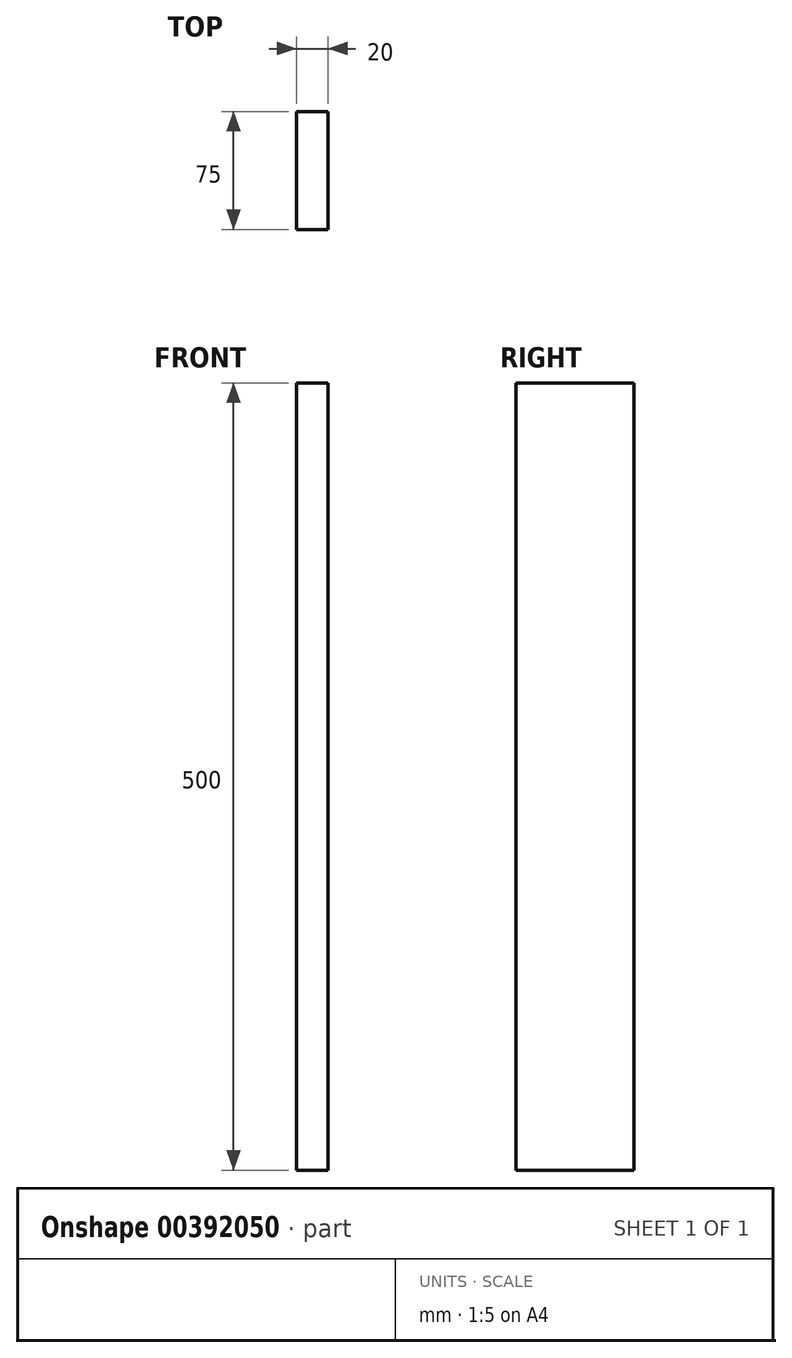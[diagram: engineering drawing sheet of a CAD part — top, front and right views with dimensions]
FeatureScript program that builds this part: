
annotation { "Feature Type Name" : "Feature", "Feature Type Description" : "" }
export const myFeature = defineFeature(function(context is Context, id is Id, definition is map)
    precondition{}
    {
        {
            var Q0;
            Q0=qCreatedBy(makeId("Top.planeOp"),FACE);
            var sketch = newSketch(context, id + "F0", { "sketchPlane" : qUnion([Q0])});
            skLineSegment(sketch, "E0.bottom", {"start": v(-10, -37.5) * mm, "end": v(10, -37.5) * mm});
            skLineSegment(sketch, "E0.top", {"start": v(-10, 37.5) * mm, "end": v(10, 37.5) * mm});
            skLineSegment(sketch, "E0.left", {"start": v(-10, -37.5) * mm, "end": v(-10, 37.5) * mm});
            skLineSegment(sketch, "E0.right", {"start": v(10, -37.5) * mm, "end": v(10, 37.5) * mm});
            skPoint(sketch, "E0.middle", {"position": v(0, 0) * mm});
            skSolve(sketch);
        }
        {
            var Q0;
            Q0=makeQuery(id+"F0.imprint","IMPRINT",FACE,{"disambiguationData":[TD([[makeQuery(id+"F0.imprint","IMPRINT",EDGE,{"derivedFrom":sQuery(id+"F0.wireOp",EDGE,"E0.bottom")}),1.0]])]});
            extrude(context, id + "F1", {"entities" : qUnion([Q0]), "endBound" : BoundingType.SYMMETRIC, "depth" : 500 * mm});
        }
    });
